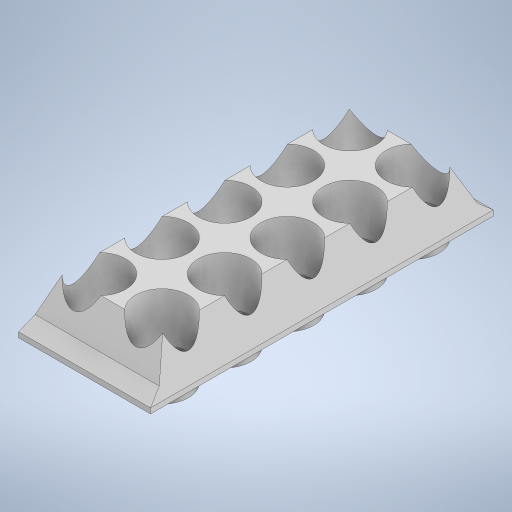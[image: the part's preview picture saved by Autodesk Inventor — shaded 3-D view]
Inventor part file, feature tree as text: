
AUTODESK INVENTOR PART (.ipt)
format: ipt  version: 2023 (Build 270158000, 158)  size: 438,272 bytes
history: native  units: mm
features: extrude x4, sketch x3, shell x1
ambient origin geometry x8: Origin, YZ Plane, XZ Plane, XY Plane, X Axis, Y Axis, Z Axis, Center Point
bodies: Solid1 (feature_tree)
feature tree (8):
  extrude  "Extrusion1"  Depth=95.0mm
  extrude  "Extrusion2"  Depth=20.071286mm
  sketch  "Sketch4"  dims[d8=260.0mm d9=20.071286mm d10=75.0mm d11=200.0mm d12=0.0mm d13=3.490659mm d14=3.490659mm d15=200.0mm d16=0.0mm d17=80.0mm d18=80.0mm d19=80.0mm d20=80.0mm d21=80.0mm d22=80.0mm d23=80.0mm d24=80.0mm d25=80.0mm d26=80.0mm d27=95.0mm d29=52.5mm d32=95.0mm d33=70.0mm d34=95.0mm d35=95.0mm d36=95.0mm d37=0.0mm d38=0.0mm d39=20.0mm d40=0.0mm d41=1.0mm]
  extrude  "Extrusion3"  Depth=1.0mm
  extrude  "Extrusion4"  Depth=75.0mm
  shell  "Shell1"  Thickness=200.0mm
  sketch  "Sketch1"  dims[d2=520.0mm d3=95.0mm d4=8.0mm]
  sketch  "Sketch3"  dims[d5=22.68928mm d6=20.071286mm d7=25.0mm]
